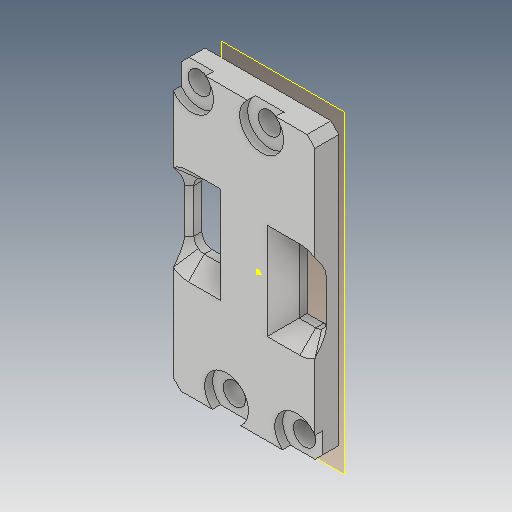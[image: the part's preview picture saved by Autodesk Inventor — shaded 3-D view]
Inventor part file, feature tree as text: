
AUTODESK INVENTOR PART (.ipt)
format: ipt  version: 2019 (Build 230136000, 136)  size: 220,672 bytes
history: native  units: mm
features: reference x9, other x8, sketch x3, plane x1, extrude x1, hole x1, chamfer x1
ambient origin geometry x8: Origin, YZ Plane, XZ Plane, XY Plane, X Axis, Y Axis, Z Axis, Center Point
bodies: Volumenkörper1 (feature_tree)
feature tree (24):
  plane  "Arbeitsebene1"
  extrude  "Extrusion1"  Depth=0.3mm
  sketch  "Skizze2"  dims[d2=3.0mm d3=0.0mm]
  hole  "Bohrung1"  [1 undecoded]
  chamfer  "Fase1"  [1 undecoded]
  sketch  "Skizze1"  dims[d0=0.3mm d1=0.3mm]
  reference  "Referenz1"
  reference  "Referenz2"
  reference  "Referenz3"
  reference  "Referenz4"
  reference  "Referenz5"
  sketch  "Skizze3"  dims[d4=2.8mm d5=6.0mm d6=5.5mm d7=1.0mm d8=90.0deg d9=12.0mm d10=20.594885mm d11=2.0mm d12=2.0mm d13=45.0deg]
  reference  "Referenz6"
  reference  "Referenz7"
  reference  "Referenz8"
  reference  "Referenz9"
  other  "<userpath>\Documents\Inventor\HITscope\Assembly_HITscope.iam"
  other  "Assembly_HITscope.iam"
  other  "HITscope_v0:1"
  other  "01_Camera_Module_v0:1"
  other  "HITscope_v0:3"
  other  "00_ESP32_Board:1"
  other  "<userpath>\Documents\Inventor\HITscope\HITscope_v0.iam"
  other  "HITscope_v0.iam"
note: 2 required parameter values undecoded (feature->parameter linkage not recoverable at this tier; creation-order binding heuristic only, values carry confidence <= 0.55)
